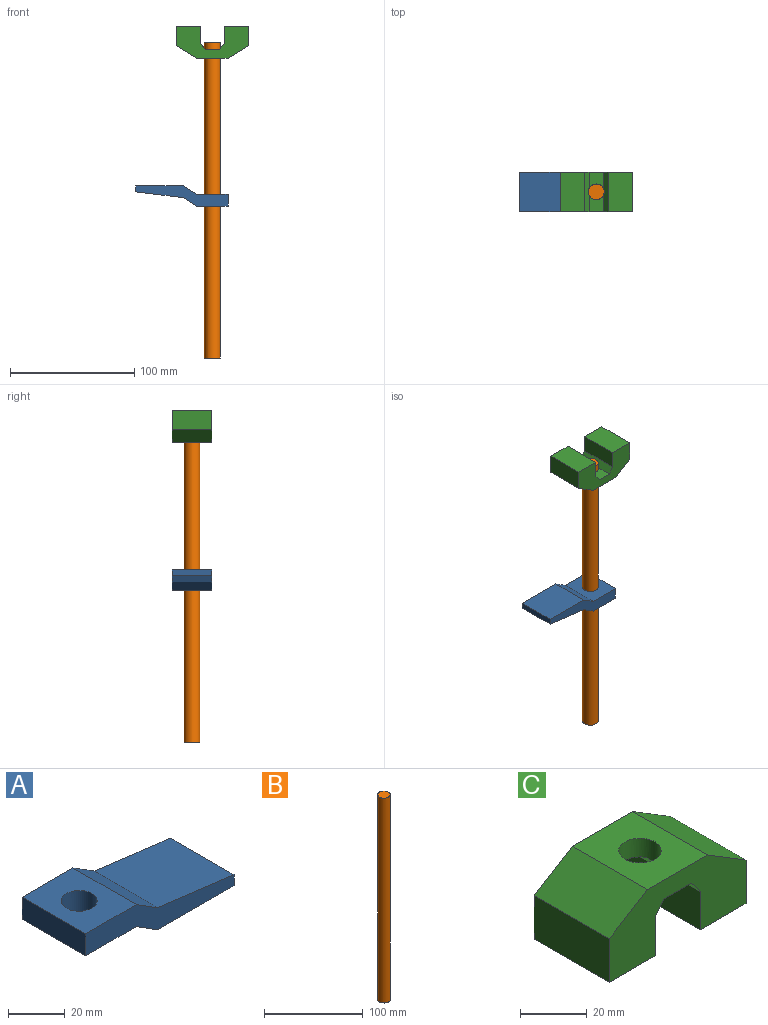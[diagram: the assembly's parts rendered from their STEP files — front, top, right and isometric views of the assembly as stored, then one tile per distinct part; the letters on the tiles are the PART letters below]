
ASSEMBLY  parts=3 mates=1
PART A: 11 faces, bbox 74.2x31.8x16.3 mm
  f0: plane 38.1x31.75mm, normal (0,0,-1), area 1209.7mm2, adj f1,f7,f8,f9
  f1: plane 31.75x4.76mm, normal (1,0,0), area 151.2mm2, adj f0,f2,f8,f9
  f2: plane 38.1x31.75mm, normal (0.12,0,0.99), area 1219.1mm2, adj f1,f3,f8,f9
  f3: plane 31.75x10.75mm, normal (0.53,0,0.85), area 403.2mm2, adj f2,f4,f8,f9
  f4: plane 31.75x25.4mm, normal (0,0,1), area 679.8mm2, adj f3,f5,f8,f9,f10
  f5: plane 31.75x9.53mm, normal (-1,0,0), area 302.4mm2, adj f4,f6,f8,f9
  f6: plane 31.75x25.4mm, normal (0,0,-1), area 679.8mm2, adj f5,f7,f8,f9,f10
  f7: plane 31.75x10.75mm, normal (-0.53,0,-0.85), area 403.2mm2, adj f0,f6,f8,f9
  f8: plane 74.25x16.29mm, normal (0,-1,0), area 616.5mm2, adj f0,f1,f2,f3,f4,f5,f6,f7
  f9: plane 74.25x16.29mm, normal (0,1,0), area 616.5mm2, adj f0,f1,f2,f3,f4,f5,f6,f7
  f10: cylinder r=6.35mm len=12.7mm, axis (0,0,1), area 380mm2, adj f4,f6
PART B: 3 faces, bbox 12.7x12.7x254 mm
  f0: cylinder r=6.35mm len=254mm, axis (0,0,-1), area 10134.1mm2, adj f1,f2
  f1: plane 12.7x12.7mm, normal (0,0,1), area 126.7mm2, adj f0
  f2: plane 12.7x12.7mm, normal (0,0,-1), area 126.7mm2, adj f0
PART C: 16 faces, bbox 57.9x31.8x25.9 mm
  f0: plane 31.75x19.4mm, normal (0,0,-1), area 616.1mm2, adj f1,f4,f8,f14
  f1: plane 57.86x25.85mm, normal (0,1,0), area 990.3mm2, adj f0,f2,f3,f4,f5,f6,f7,f10
  f2: plane 31.75x15.88mm, normal (-1,0,0), area 504mm2, adj f1,f3,f7,f8
  f3: plane 31.75x19.4mm, normal (0,0,-1), area 616.1mm2, adj f1,f2,f8,f15
  f4: plane 31.75x15.88mm, normal (1,0,0), area 504mm2, adj f0,f1,f5,f8
  f5: plane 31.75x16.23mm, normal (0.52,0,0.85), area 604.8mm2, adj f1,f4,f6,f8
  f6: plane 31.75x25.4mm, normal (0,0,1), area 679.8mm2, adj f1,f5,f7,f8,f9
  f7: plane 31.75x16.23mm, normal (-0.52,0,0.85), area 604.8mm2, adj f1,f2,f6,f8
  f8: plane 57.86x25.85mm, normal (0,-1,0), area 990.3mm2, adj f0,f2,f3,f4,f5,f6,f7,f10
  f9: cylinder r=6.35mm len=12.7mm, axis (0,0,1), area 277.8mm2, adj f6,f10,f11,f12,f13
  f10: plane 31.75x5.08mm, normal (-0.8,0,-0.6), area 197.7mm2, adj f1,f8,f9,f12,f13,f14
  f11: plane 31.75x5.08mm, normal (0.8,0,-0.6), area 197.7mm2, adj f1,f8,f9,f12,f13,f15
  f12: plane 13.11x11.43mm, normal (0,0,-1), area 120.5mm2, adj f8,f9,f10,f11
  f13: plane 13.11x11.43mm, normal (0,0,-1), area 120.5mm2, adj f1,f9,f10,f11
  f14: plane 31.75x13.97mm, normal (-1,0,0), area 443.5mm2, adj f0,f1,f8,f10
  f15: plane 31.75x13.97mm, normal (1,0,0), area 443.5mm2, adj f1,f3,f8,f11
PLACE A rot(axis=(0,1,0),180deg) t=(-9.4,8.2,70.81)mm
PLACE B t=(-22.1,-7.67,-51.42)mm
PLACE C rot(axis=(1,0,0),180deg) t=(-22.1,-23.55,215.73)mm fixed
MATE slider B.f0 <-> A.f10  axis (0,0,-1) through (-22.1,-7.67,75.58)mm
